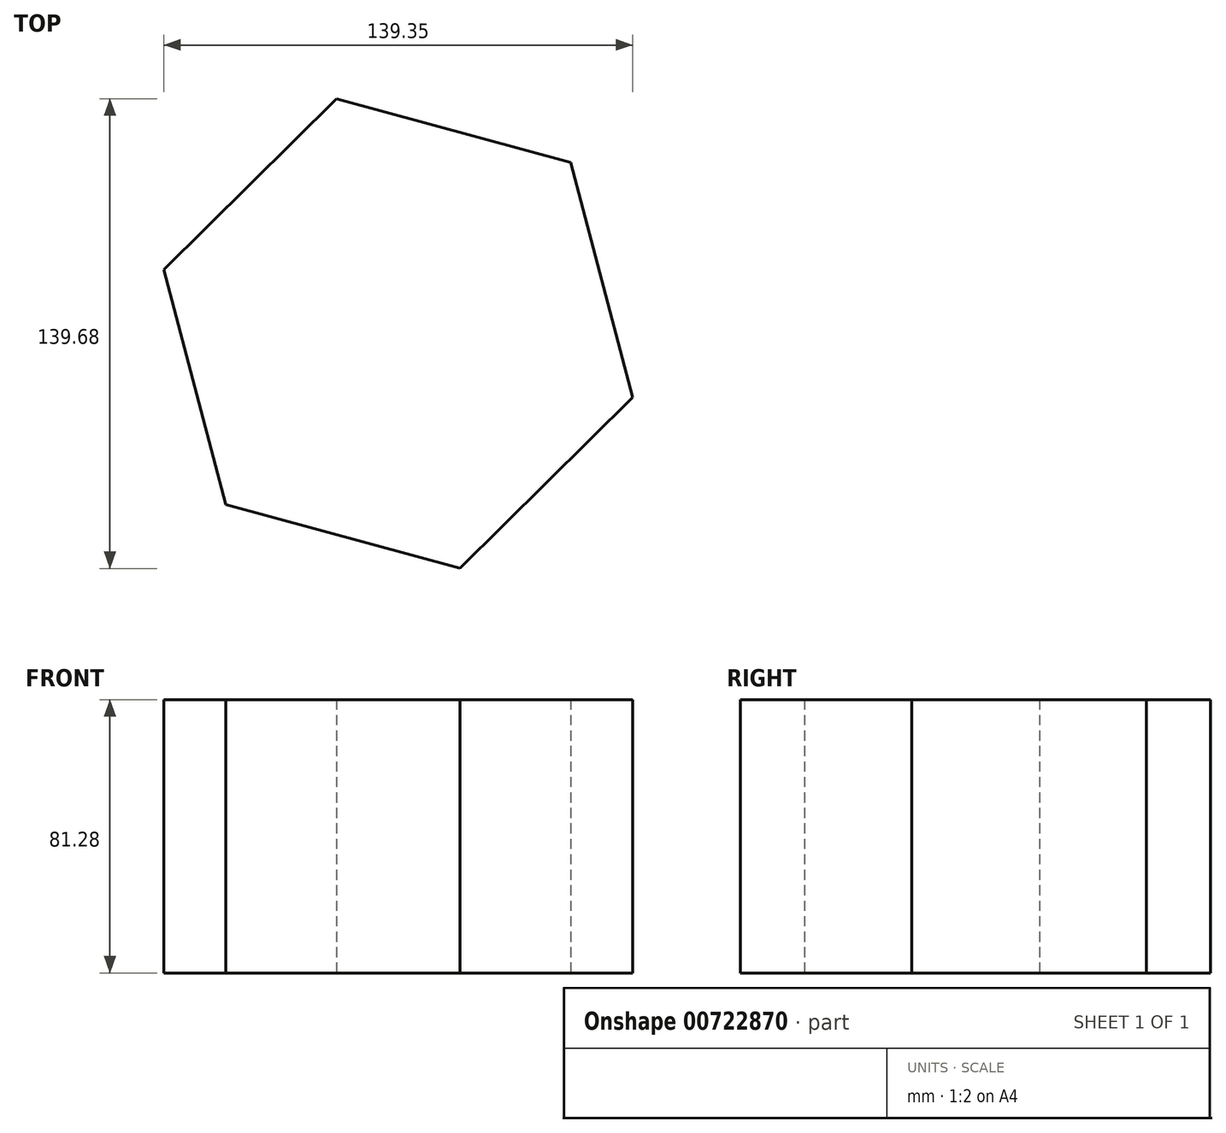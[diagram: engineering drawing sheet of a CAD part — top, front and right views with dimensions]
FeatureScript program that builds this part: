
annotation { "Feature Type Name" : "Feature", "Feature Type Description" : "" }
export const myFeature = defineFeature(function(context is Context, id is Id, definition is map)
    precondition{}
    {
        {
            var Q0;
            Q0=qCreatedBy(makeId("Top.planeOp"),FACE);
            var sketch = newSketch(context, id + "F0", { "sketchPlane" : qUnion([Q0])});
            skCircle(sketch, "E0.cCircle", {"center": v(2.85, 0) * mm, "radius": 62.54 * mm, "construction": true});
            skLineSegment(sketch, "E0.0", {"start": v(72.52, -19) * mm, "end": v(21.24, -69.84) * mm});
            skLineSegment(sketch, "E0.1", {"start": v(21.24, -69.84) * mm, "end": v(-48.44, -50.85) * mm});
            skLineSegment(sketch, "E0.2", {"start": v(-48.44, -50.85) * mm, "end": v(-66.83, 19) * mm});
            skLineSegment(sketch, "E0.3", {"start": v(-66.83, 19) * mm, "end": v(-15.54, 69.84) * mm});
            skLineSegment(sketch, "E0.4", {"start": v(-15.54, 69.84) * mm, "end": v(54.13, 50.85) * mm});
            skLineSegment(sketch, "E0.5", {"start": v(54.13, 50.85) * mm, "end": v(72.52, -19) * mm});
            skPoint(sketch, "E0.0.midPoint", {"position": v(46.88, -44.41) * mm});
            skSolve(sketch);
        }
        {
            var Q0;
            Q0 = qSketchRegion(id + "F0", true);
            extrude(context, id + "F1", {"entities" : qUnion([Q0]), "depth" : 81.28 * mm, "offsetDistance" : 25.4 * mm});
        }
    });
